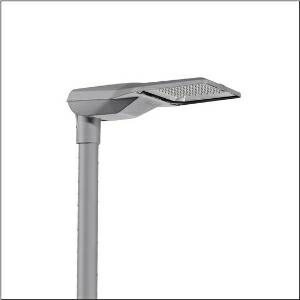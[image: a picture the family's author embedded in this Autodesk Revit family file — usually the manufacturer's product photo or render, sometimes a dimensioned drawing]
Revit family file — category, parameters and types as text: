
# Revit family: streetlight_sl_21_iq_midi___stw1_0a_5xe3e21g08nb_ca38
name_source: partatom
category: Lighting Fixtures
units: mm (PartAtom-declared; Revit-internal decimal feet)

## family parameters
Cut with Voids When Loaded = No
Host = Face
Light Source = No
Part Type = Normal
Room Calculation Point = No
Round Connector Dimension = Use Diameter
Shared = No

## types (1)
- --- (1 x LED, 19210 lm, 155.5 W, 2200K)
    Apparent Load = 155 VA
    CIE Flux Codes = 39 75 98 100 100
    Color Rendering = 70
    Color Temperature = 2200K
    Default Elevation = 1800 mm
    Description = Streetlight SL 21 iQ midi, mast luminaire, primary light control with lens, of PMMA, primary optical cover: cover, of toughened safety glass, transparent, light distribution: STW1.0a, light emission: direct distribution, primary light characteristic: asymmetric, installation type: post-top, side-entry, LED, High Power LED, rated luminous flux: 19.210lm, luminous efficacy: 124lm/W, light colour: 722, colour temperature: 2200K, control gear: iQ Street-Remote, control: Street-Remote, Auto-Match, Temp-Guard, Lumen-Switch, Night-Set, Smart-Wire, Light-Fading, Desk-Remote (wireless, voltage-free reading and setting of iQ features in the workshop via application-optimized NFC function/RFID function), optimised constant luminous flux control (CLO 2.0), pre-setting: linear dimming characteristic, mains connection: 230..240V, AC, 50/60Hz, start of lifetime: 156W, end of service life: 162W, reduction: 69W, luminaire housing, of diecast aluminium, powder-coated, Siteco® metallic grey (DB 702S), corrosivity category C5 mid according to DIN EN ISO 12944, please order mast flange separately, inclination adjustable: 0°, 5°, 10°, 15°, sealing non-destructively replaceable, multi-level sealing system, length: 644mm, width: 335mm, height: 110mm, mast flange for spigot size: 42mm (side-entry): 5XC10008XM4, 60/48mm (side-entry/post-top): 5XC10108XM2, 76/60mm (side-entry/post-top): 5XC10108XM1, mounting height: 4..8m, protection rating (complete): IP66, insulation class (complete): insulation class II (safety insulation), certification: CE, ENEC, ENEC+, VDE, impact resistance: IK10, permissible operating ambient temperature for outdoor applications: -40..+50°C, standard-compliant lighting for roads and squares, packaging unit: 1 piece

Light Distribution: STW1.0a
    Height = 111 mm
    Lamp = 1 x LED
    Lamp Light Flux = 19210 lm
    Lamp Power = 155.5 W
    Lamp count = 1
    Length = 644 mm
    Luminous efficacy = 124 lm/W
    Manufacturer = Siteco
    ModVariant = No
    Model = 5XE3E21G08NB
    Number of Poles = 1
    OnlyDefault = Yes
    Power Factor = 1
    Product Name = Streetlight SL 21 iQ midi | STW1.0a
    Product group = mast luminaire | pylon top
    ProductGroupID = 6100
    Protection Class = Protection class II
    Protection Degree = IP 66
    RLX_Detail_Level = 1
    RLX_Emergency_Light_Flux = 0 lm
    RLX_Emergency_Type = 0
    RLX_Emergency_Type_DB = No
    RlxData = <blob elided: 27285 chars, md5=85ebe393>
    Socket = socket
    Standby Power = 0 W
    System Light Flux = 19210 lm
    System Power = 155 W
    Type Comments = factory setting: luminous flux: 100 % | dim-lin: 254 | 823 mA
    Type Image = l_1004298.jpg
    URL = http://relux.com
    VarID = @adj_191429
    Voltage = 0 V
    Weight = 0.00 kg
    Width = 336 mm

## geometry (parser evidence)
native form markers: Blend x4, Sweep x11
no freeform markers — native parametric forms only
